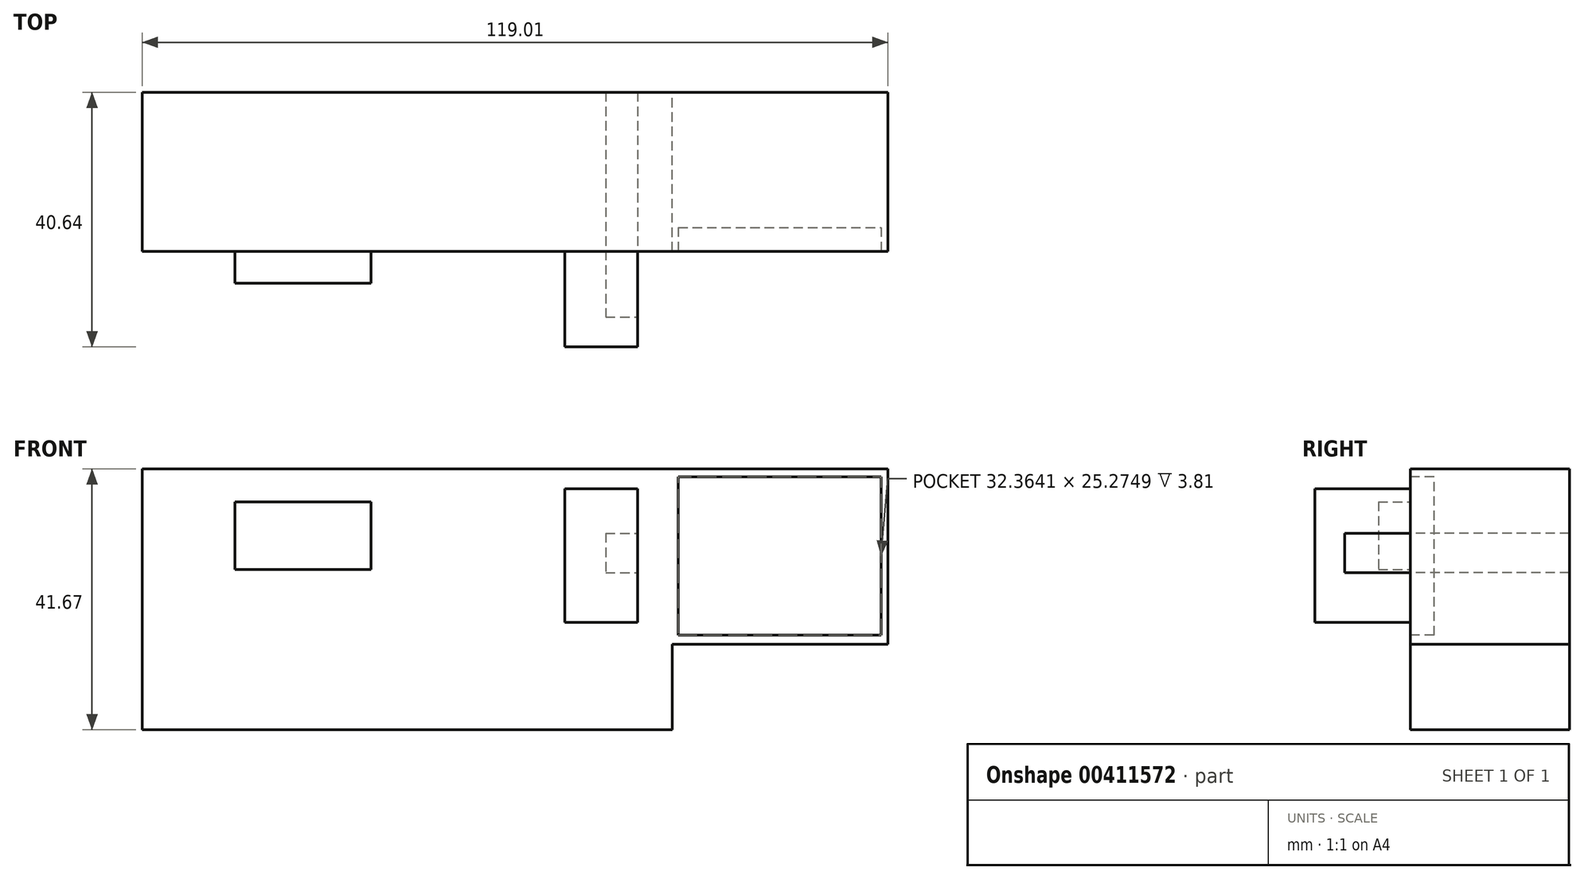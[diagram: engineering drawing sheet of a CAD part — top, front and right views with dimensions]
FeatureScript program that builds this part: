
annotation { "Feature Type Name" : "Feature", "Feature Type Description" : "" }
export const myFeature = defineFeature(function(context is Context, id is Id, definition is map)
    precondition{}
    {
        {
            var Q0;
            Q0=qCreatedBy(makeId("Front.planeOp"),FACE);
            var sketch = newSketch(context, id + "F0", { "sketchPlane" : qUnion([Q0])});
            skLineSegment(sketch, "E0.bottom", {"start": v(-39.3, 17.7) * mm, "end": v(45.3, 17.7) * mm});
            skLineSegment(sketch, "E0.top", {"start": v(-39.3, -23.97) * mm, "end": v(45.3, -23.97) * mm});
            skLineSegment(sketch, "E0.left", {"start": v(-39.3, 17.7) * mm, "end": v(-39.3, -23.97) * mm});
            skLineSegment(sketch, "E0.right", {"start": v(45.3, 17.7) * mm, "end": v(45.3, -23.97) * mm});
            skLineSegment(sketch, "E1.bottom", {"start": v(45.3, 17.7) * mm, "end": v(79.71, 17.7) * mm});
            skLineSegment(sketch, "E1.top", {"start": v(45.3, -10.31) * mm, "end": v(79.71, -10.31) * mm});
            skLineSegment(sketch, "E1.left", {"start": v(45.3, 17.7) * mm, "end": v(45.3, -10.31) * mm});
            skLineSegment(sketch, "E1.right", {"start": v(79.71, 17.7) * mm, "end": v(79.71, -10.31) * mm});
            skSolve(sketch);
        }
        {
            var Q0;
            Q0=makeQuery(id+"F0.imprint","IMPRINT",FACE,{"disambiguationData":[TD([[makeQuery(id+"F0.imprint","IMPRINT",EDGE,{"derivedFrom":sQuery(id+"F0.wireOp",EDGE,"E0.bottom")}),-1.0]])]});
            var Q1;
            Q1=makeQuery(id+"F0.imprint","IMPRINT",FACE,{"disambiguationData":[TD([[makeQuery(id+"F0.imprint","IMPRINT",EDGE,{"derivedFrom":sQuery(id+"F0.wireOp",EDGE,"E1.bottom")}),-1.0]])]});
            extrude(context, id + "F1", {"entities" : qUnion([Q0, Q1]), "depth" : 25.4 * mm});
        }
        {
            var Q0;
            Q0=makeQuery(id+"F1.opExtrude","CAP_FACE",FACE,{"disambiguationData":[OSD([sQuery(id+"F0.wireOp",EDGE,"E0.bottom"),sQuery(id+"F0.wireOp",EDGE,"E0.top"),sQuery(id+"F0.wireOp",EDGE,"E0.left"),sQuery(id+"F0.wireOp",EDGE,"E0.right"),sQuery(id+"F0.wireOp",EDGE,"E1.bottom"),sQuery(id+"F0.wireOp",EDGE,"E1.top"),sQuery(id+"F0.wireOp",EDGE,"E1.right")])],"isStart":false});
            var sketch = newSketch(context, id + "F2", { "sketchPlane" : qUnion([Q0])});
            skLineSegment(sketch, "E2.bottom", {"start": v(-24.5, 12.45) * mm, "end": v(-2.78, 12.45) * mm});
            skLineSegment(sketch, "E2.top", {"start": v(-24.5, 1.64) * mm, "end": v(-2.78, 1.64) * mm});
            skLineSegment(sketch, "E2.left", {"start": v(-24.5, 12.45) * mm, "end": v(-24.5, 1.64) * mm});
            skLineSegment(sketch, "E2.right", {"start": v(-2.78, 12.45) * mm, "end": v(-2.78, 1.64) * mm});
            skSolve(sketch);
        }
        {
            var Q0;
            Q0 = qSketchRegion(id + "F2", true);
            extrude(context, id + "F3", {"entities" : qUnion([Q0]), "operationType" : NewBodyOperationType.ADD, "depth" : 5.08 * mm});
        }
        {
            var Q0;
            Q0=makeQuery(id+"F1.opExtrude","CAP_FACE",FACE,{"disambiguationData":[OSD([sQuery(id+"F0.wireOp",EDGE,"E0.bottom"),sQuery(id+"F0.wireOp",EDGE,"E0.top"),sQuery(id+"F0.wireOp",EDGE,"E0.left"),sQuery(id+"F0.wireOp",EDGE,"E0.right"),sQuery(id+"F0.wireOp",EDGE,"E1.bottom"),sQuery(id+"F0.wireOp",EDGE,"E1.top"),sQuery(id+"F0.wireOp",EDGE,"E1.right")])],"isStart":false});
            var sketch = newSketch(context, id + "F4", { "sketchPlane" : qUnion([Q0])});
            skLineSegment(sketch, "E3.bottom", {"start": v(46.25, -8.87) * mm, "end": v(78.62, -8.87) * mm});
            skLineSegment(sketch, "E3.top", {"start": v(46.25, 16.4) * mm, "end": v(78.62, 16.4) * mm});
            skLineSegment(sketch, "E3.left", {"start": v(46.25, -8.87) * mm, "end": v(46.25, 16.4) * mm});
            skLineSegment(sketch, "E3.right", {"start": v(78.62, -8.87) * mm, "end": v(78.62, 16.4) * mm});
            skSolve(sketch);
        }
        {
            var Q0;
            Q0=makeQuery(id+"F4.imprint","IMPRINT",FACE,{"disambiguationData":[TD([[makeQuery(id+"F4.imprint","IMPRINT",EDGE,{"derivedFrom":sQuery(id+"F4.wireOp",EDGE,"E3.bottom")}),1.0]])]});
            extrude(context, id + "F5", {"entities" : qUnion([Q0]), "operationType" : NewBodyOperationType.REMOVE, "oppositeDirection" : true, "depth" : 3.8 * mm});
        }
        {
            var Q0;
            Q0=makeQuery(id+"F1.opExtrude","CAP_FACE",FACE,{"disambiguationData":[OSD([sQuery(id+"F0.wireOp",EDGE,"E0.bottom"),sQuery(id+"F0.wireOp",EDGE,"E0.top"),sQuery(id+"F0.wireOp",EDGE,"E0.left"),sQuery(id+"F0.wireOp",EDGE,"E0.right"),sQuery(id+"F0.wireOp",EDGE,"E1.bottom"),sQuery(id+"F0.wireOp",EDGE,"E1.top"),sQuery(id+"F0.wireOp",EDGE,"E1.right")])],"isStart":false});
            var sketch = newSketch(context, id + "F6", { "sketchPlane" : qUnion([Q0])});
            skLineSegment(sketch, "E4.bottom", {"start": v(39.77, 14.51) * mm, "end": v(28.16, 14.51) * mm});
            skLineSegment(sketch, "E4.top", {"start": v(39.77, -6.83) * mm, "end": v(28.16, -6.83) * mm});
            skLineSegment(sketch, "E4.left", {"start": v(39.77, 14.51) * mm, "end": v(39.77, -6.83) * mm});
            skLineSegment(sketch, "E4.right", {"start": v(28.16, 14.51) * mm, "end": v(28.16, -6.83) * mm});
            skSolve(sketch);
        }
        {
            var Q0;
            Q0 = qSketchRegion(id + "F6", true);
            extrude(context, id + "F7", {"entities" : qUnion([Q0]), "operationType" : NewBodyOperationType.ADD, "depth" : 15.24 * mm});
        }
        {
            var Q0;
            Q0=makeQuery(id+"F7.opExtrude","SWEPT_FACE",FACE,{"disambiguationData":[OSD([sQuery(id+"F6.wireOp",EDGE,"E4.left")])]});
            var sketch = newSketch(context, id + "F8", { "sketchPlane" : qUnion([Q0])});
            skLineSegment(sketch, "E5.bottom", {"start": v(-25.4, 1.13) * mm, "end": v(-35.86, 1.13) * mm});
            skLineSegment(sketch, "E5.top", {"start": v(-25.4, 7.42) * mm, "end": v(-35.86, 7.42) * mm});
            skLineSegment(sketch, "E5.left", {"start": v(-25.4, 1.13) * mm, "end": v(-25.4, 7.42) * mm});
            skLineSegment(sketch, "E5.right", {"start": v(-35.86, 1.13) * mm, "end": v(-35.86, 7.42) * mm});
            skSolve(sketch);
        }
        {
            var Q0;
            Q0 = qSketchRegion(id + "F8", true);
            extrude(context, id + "F9", {"entities" : qUnion([Q0]), "operationType" : NewBodyOperationType.REMOVE, "oppositeDirection" : true, "depth" : 5.08 * mm});
        }
        {
            var Q0;
            Q0=makeQuery(id+"F9.boolean.opBoolean","MERGE",FACE,{"derivedFrom":[makeQuery(id+"F1.opExtrude","CAP_FACE",FACE,{"disambiguationData":[OSD([sQuery(id+"F0.wireOp",EDGE,"E0.bottom"),sQuery(id+"F0.wireOp",EDGE,"E0.top"),sQuery(id+"F0.wireOp",EDGE,"E0.left"),sQuery(id+"F0.wireOp",EDGE,"E0.right"),sQuery(id+"F0.wireOp",EDGE,"E1.bottom"),sQuery(id+"F0.wireOp",EDGE,"E1.top"),sQuery(id+"F0.wireOp",EDGE,"E1.right")])],"isStart":false}),makeQuery(id+"F9.opExtrude","SWEPT_FACE",FACE,{"disambiguationData":[OSD([sQuery(id+"F8.wireOp",EDGE,"E5.left")])]})]});
            var sketch = newSketch(context, id + "F10", { "sketchPlane" : qUnion([Q0])});
            skLineSegment(sketch, "E6.bottom", {"start": v(34.69, 1.13) * mm, "end": v(39.77, 1.13) * mm});
            skLineSegment(sketch, "E6.top", {"start": v(34.69, 7.42) * mm, "end": v(39.77, 7.42) * mm});
            skLineSegment(sketch, "E6.left", {"start": v(34.69, 1.13) * mm, "end": v(34.69, 7.42) * mm});
            skLineSegment(sketch, "E6.right", {"start": v(39.77, 1.13) * mm, "end": v(39.77, 7.42) * mm});
            skSolve(sketch);
        }
        {
            var Q0;
            Q0 = qSketchRegion(id + "F10", true);
            extrude(context, id + "F11", {"entities" : qUnion([Q0]), "operationType" : NewBodyOperationType.REMOVE, "oppositeDirection" : true, "depth" : 25.4 * mm});
        }
    });
